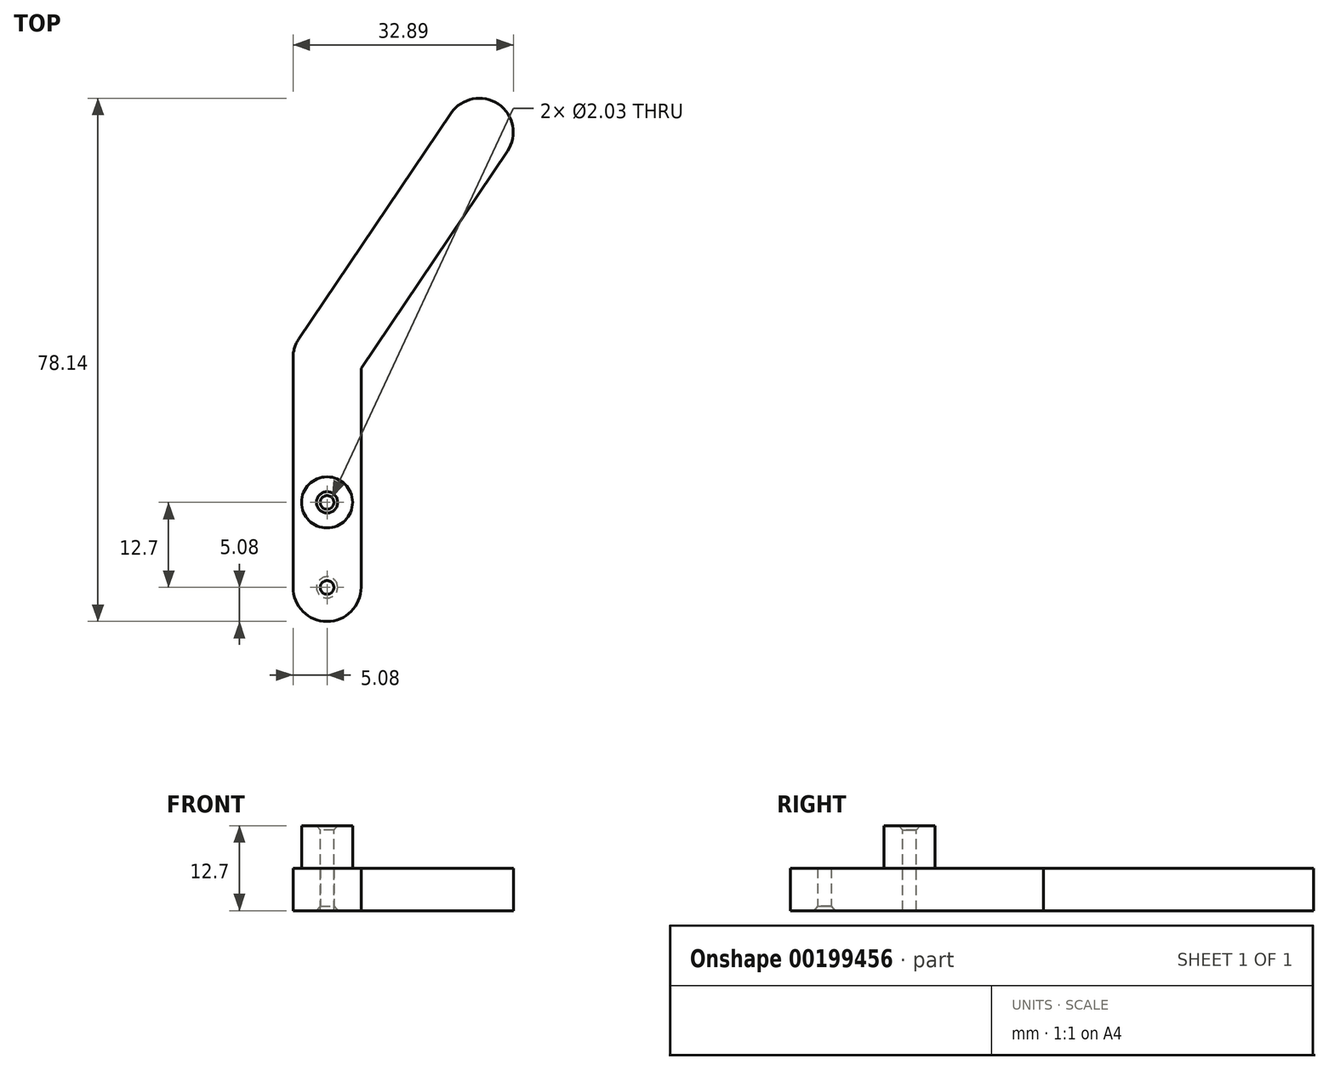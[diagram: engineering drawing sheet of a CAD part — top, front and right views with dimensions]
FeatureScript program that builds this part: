
annotation { "Feature Type Name" : "Feature", "Feature Type Description" : "" }
export const myFeature = defineFeature(function(context is Context, id is Id, definition is map)
    precondition{}
    {
        {
            var Q0;
            Q0=qCreatedBy(makeId("Top.planeOp"),FACE);
            var sketch = newSketch(context, id + "F0", { "sketchPlane" : qUnion([Q0])});
            skLineSegment(sketch, "E0", {"start": v(0, 0) * mm, "end": v(0, 12.7) * mm});
            skLineSegment(sketch, "E1", {"start": v(0, 12.7) * mm, "end": v(0, 34.3) * mm});
            skLineSegment(sketch, "E2", {"start": v(0, 34.29) * mm, "end": v(22.73, 67.98) * mm});
            skArc(sketch, "E3.0.startCap", {"start": v(4.21, 31.45) * mm, "mid": v(-2.84, 30.08) * mm, "end": v(-4.21, 37.13) * mm});
            skArc(sketch, "E3.0.endCap", {"start": v(18.51, 70.82) * mm, "mid": v(25.57, 72.2) * mm, "end": v(26.94, 65.14) * mm});
            skLineSegment(sketch, "E3.0.left", {"start": v(-4.21, 37.13) * mm, "end": v(18.51, 70.82) * mm});
            skLineSegment(sketch, "E3.0.right", {"start": v(4.21, 31.45) * mm, "end": v(26.94, 65.14) * mm});
            skArc(sketch, "E3.1.startCap", {"start": v(5.08, 12.7) * mm, "mid": v(0, 7.62) * mm, "end": v(-5.08, 12.7) * mm});
            skArc(sketch, "E3.1.endCap", {"start": v(-5.08, 34.3) * mm, "mid": v(0, 39.37) * mm, "end": v(5.08, 34.3) * mm});
            skLineSegment(sketch, "E3.1.left", {"start": v(-5.08, 12.7) * mm, "end": v(-5.08, 34.3) * mm});
            skLineSegment(sketch, "E3.1.right", {"start": v(5.08, 12.7) * mm, "end": v(5.08, 34.3) * mm});
            skArc(sketch, "E3.2.startCap", {"start": v(5.08, 0) * mm, "mid": v(0, -5.08) * mm, "end": v(-5.08, 0) * mm});
            skArc(sketch, "E3.2.endCap", {"start": v(-5.08, 12.7) * mm, "mid": v(0, 17.78) * mm, "end": v(5.08, 12.7) * mm});
            skLineSegment(sketch, "E3.2.left", {"start": v(-5.08, 0) * mm, "end": v(-5.08, 12.7) * mm});
            skLineSegment(sketch, "E3.2.right", {"start": v(5.08, 0) * mm, "end": v(5.08, 12.7) * mm});
            skSolve(sketch);
        }
        {
            var Q0;
            Q0 = qSketchRegion(id + "F0", true);
            extrude(context, id + "F1", {"entities" : qUnion([Q0]), "depth" : 6.35 * mm});
        }
        {
            var Q0;
            Q0=qCreatedBy(makeId("Top.planeOp"),FACE);
            var sketch = newSketch(context, id + "F2", { "sketchPlane" : qUnion([Q0])});
            skCircle(sketch, "E4", {"center": v(0, 12.7) * mm, "radius": 3.81 * mm});
            skSolve(sketch);
        }
        {
            var Q0;
            Q0 = qSketchRegion(id + "F2", true);
            extrude(context, id + "F3", {"entities" : qUnion([Q0]), "operationType" : NewBodyOperationType.ADD, "depth" : 12.7 * mm});
        }
        {
            var Q0;
            Q0=makeQuery(id+"F3.opExtrude","CAP_FACE",FACE,{"disambiguationData":[OSD([sQuery(id+"F2.wireOp",EDGE,"E4")])],"isStart":false});
            var sketch = newSketch(context, id + "F4", { "sketchPlane" : qUnion([Q0])});
            skPoint(sketch, "E5", {"position": v(0, 12.7) * mm});
            skSolve(sketch);
        }
        {
            var Q0;
            Q0=sQuery(id+"F4.wireOp",VERTEX,"E5");
            var Q1;
            Q1=makeQuery(id+"F1.opExtrude","SWEPT_BODY",BODY,{"disambiguationData":[OSD([sQuery(id+"F0.wireOp",EDGE,"E3.0.endCap"),sQuery(id+"F0.wireOp",EDGE,"E3.0.left"),sQuery(id+"F0.wireOp",EDGE,"E3.0.right"),sQuery(id+"F0.wireOp",EDGE,"E3.1.endCap"),sQuery(id+"F0.wireOp",EDGE,"E3.1.left"),sQuery(id+"F0.wireOp",EDGE,"E3.1.right"),sQuery(id+"F0.wireOp",EDGE,"E3.2.startCap"),sQuery(id+"F0.wireOp",EDGE,"E3.2.left"),sQuery(id+"F0.wireOp",EDGE,"E3.2.right")])]});
            hole(context, id + "F5", {"style" : HoleStyle.C_SINK, "endStyle" : HoleEndStyle.THROUGH, "holeDiameter" : 2.03 * mm, "cSinkDiameter" : 3.17 * mm, "cSinkAngle" : 82 * degree, "locations" : qUnion([Q0]), "scope" : qUnion([Q1]), "isTappedThrough" : true});
        }
        {
            var Q0;
            Q0=sQuery(id+"F0.wireOp",VERTEX,"E0.start");
            var Q1;
            Q1=makeQuery(id+"F1.opExtrude","SWEPT_BODY",BODY,{"disambiguationData":[OSD([sQuery(id+"F0.wireOp",EDGE,"E3.0.endCap"),sQuery(id+"F0.wireOp",EDGE,"E3.0.left"),sQuery(id+"F0.wireOp",EDGE,"E3.0.right"),sQuery(id+"F0.wireOp",EDGE,"E3.1.endCap"),sQuery(id+"F0.wireOp",EDGE,"E3.1.left"),sQuery(id+"F0.wireOp",EDGE,"E3.1.right"),sQuery(id+"F0.wireOp",EDGE,"E3.2.startCap"),sQuery(id+"F0.wireOp",EDGE,"E3.2.left"),sQuery(id+"F0.wireOp",EDGE,"E3.2.right")])]});
            hole(context, id + "F6", {"style" : HoleStyle.C_SINK, "endStyle" : HoleEndStyle.THROUGH, "oppositeDirection" : true, "holeDiameter" : 2.03 * mm, "cSinkDiameter" : 3.17 * mm, "cSinkAngle" : 82 * degree, "locations" : qUnion([Q0]), "scope" : qUnion([Q1]), "isTappedThrough" : true});
        }
    });
